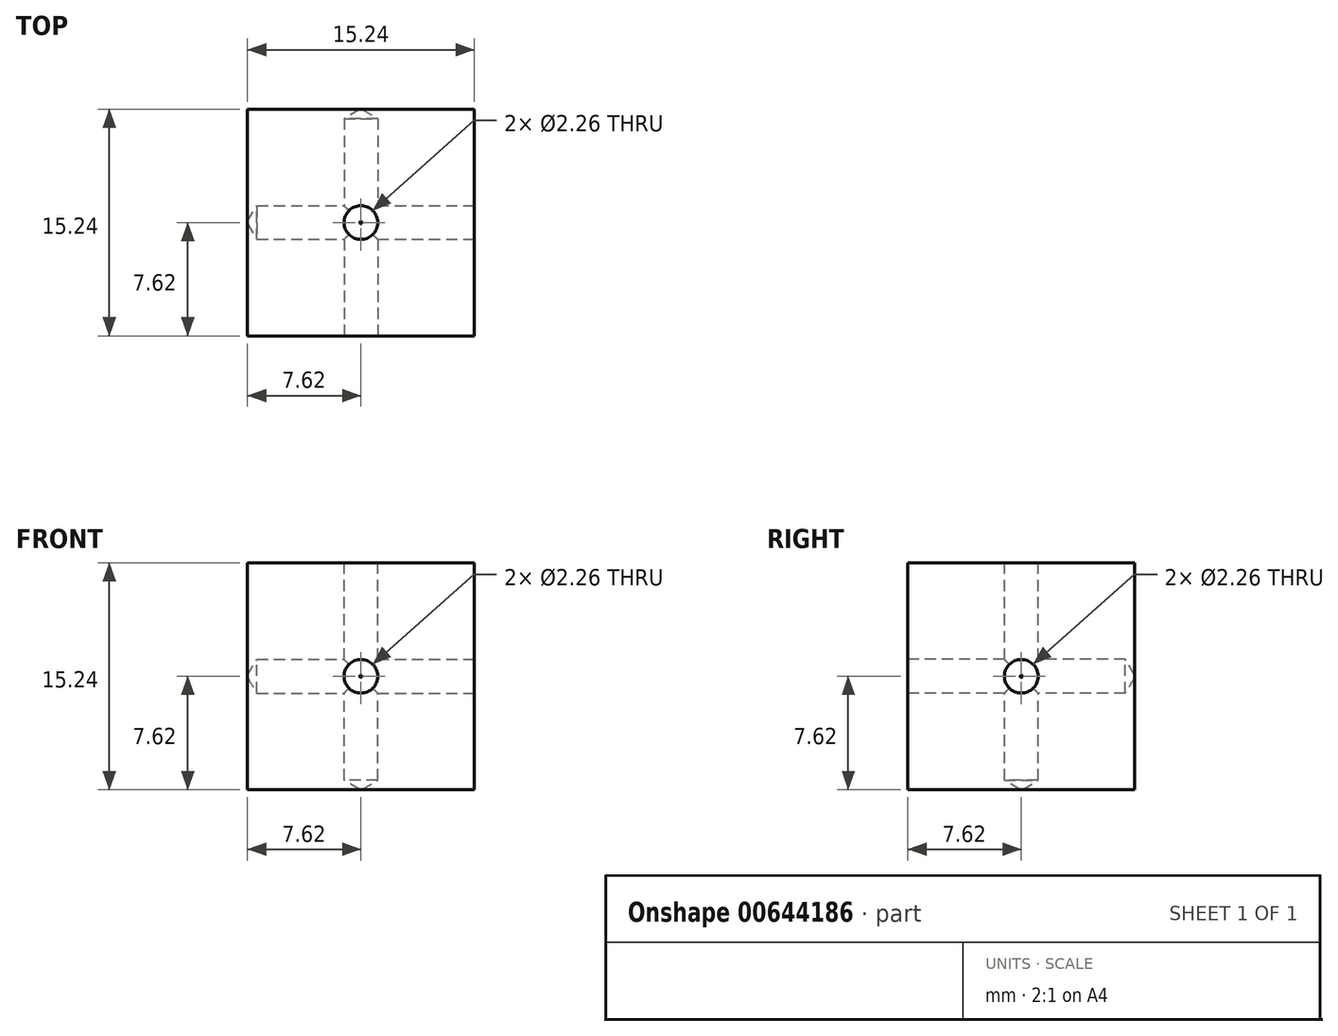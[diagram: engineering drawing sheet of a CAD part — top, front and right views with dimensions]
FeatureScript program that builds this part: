
annotation { "Feature Type Name" : "Feature", "Feature Type Description" : "" }
export const myFeature = defineFeature(function(context is Context, id is Id, definition is map)
    precondition{}
    {
        {
            var Q0;
            Q0=qCreatedBy(makeId("Front.planeOp"),FACE);
            var sketch = newSketch(context, id + "F0", { "sketchPlane" : qUnion([Q0])});
            skLineSegment(sketch, "E0.bottom", {"start": v(-7.62, 7.62) * mm, "end": v(7.62, 7.62) * mm});
            skLineSegment(sketch, "E0.top", {"start": v(-7.62, -7.62) * mm, "end": v(7.62, -7.62) * mm});
            skLineSegment(sketch, "E0.left", {"start": v(-7.62, 7.62) * mm, "end": v(-7.62, -7.62) * mm});
            skLineSegment(sketch, "E0.right", {"start": v(7.62, 7.62) * mm, "end": v(7.62, -7.62) * mm});
            skPoint(sketch, "E0.middle", {"position": v(0, 0) * mm});
            skSolve(sketch);
        }
        {
            var Q0;
            Q0=makeQuery(id+"F0.imprint","IMPRINT",FACE,{"disambiguationData":[TD([[makeQuery(id+"F0.imprint","IMPRINT",EDGE,{"derivedFrom":sQuery(id+"F0.wireOp",EDGE,"E0.bottom")}),-1.0]])]});
            extrude(context, id + "F1", {"entities" : qUnion([Q0]), "depth" : 15.24 * mm, "offsetDistance" : 25.4 * mm});
        }
        {
            var Q0;
            Q0=makeQuery(id+"F1.opExtrude","CAP_FACE",FACE,{"disambiguationData":[OSD([sQuery(id+"F0.wireOp",EDGE,"E0.bottom"),sQuery(id+"F0.wireOp",EDGE,"E0.top"),sQuery(id+"F0.wireOp",EDGE,"E0.left"),sQuery(id+"F0.wireOp",EDGE,"E0.right")])],"isStart":false});
            var sketch = newSketch(context, id + "F2", { "sketchPlane" : qUnion([Q0])});
            skPoint(sketch, "E1", {"position": v(0, 0) * mm});
            skSolve(sketch);
        }
        {
            var Q0;
            Q0=sQuery(id+"F2.wireOp",VERTEX,"E1");
            var Q1;
            Q1=makeQuery(id+"F1.opExtrude","SWEPT_BODY",BODY,{"disambiguationData":[OSD([sQuery(id+"F0.wireOp",EDGE,"E0.bottom"),sQuery(id+"F0.wireOp",EDGE,"E0.top"),sQuery(id+"F0.wireOp",EDGE,"E0.left"),sQuery(id+"F0.wireOp",EDGE,"E0.right")])]});
            hole(context, id + "F3", {"style" : HoleStyle.SIMPLE, "endStyle" : HoleEndStyle.BLIND, "standardTappedOrClearance" : lookupTablePath({ "standard" : "ANSI", "engagement" : "75%", "pitch" : "40 tpi", "size" : "#4", "type" : "Tapped" }), "standardBlindInLast" : lookupTablePath({ "standard" : "ANSI", "engagement" : "75%", "pitch" : "40 tpi", "size" : "#4", "type" : "Tapped" }), "holeDiameter" : 2.26 * mm, "majorDiameter" : 2.84 * mm, "showTappedDepth" : true, "holeDepth" : 14.6 * mm, "isTappedThrough" : true, "tappedDepth" : 12.7 * mm, "tapClearance" : 3, "locations" : qUnion([Q0]), "scope" : qUnion([Q1])});
        }
        {
            var Q0;
            Q0=makeQuery(id+"F1.opExtrude","SWEPT_FACE",FACE,{"disambiguationData":[OSD([sQuery(id+"F0.wireOp",EDGE,"E0.right")])]});
            var sketch = newSketch(context, id + "F4", { "sketchPlane" : qUnion([Q0])});
            skPoint(sketch, "E2", {"position": v(-7.62, 0) * mm});
            skPoint(sketch, "E2.positionSnap0", {"position": v(-7.62, 7.62) * mm});
            skSolve(sketch);
        }
        {
            var Q0;
            Q0=makeQuery(id+"F1.opExtrude","SWEPT_FACE",FACE,{"disambiguationData":[OSD([sQuery(id+"F0.wireOp",EDGE,"E0.bottom")])]});
            var sketch = newSketch(context, id + "F5", { "sketchPlane" : qUnion([Q0])});
            skPoint(sketch, "E3", {"position": v(0, -7.62) * mm});
            skPoint(sketch, "E3.positionSnap0", {"position": v(0, -15.24) * mm});
            skPoint(sketch, "E3.positionSnap1", {"position": v(7.62, -7.62) * mm});
            skSolve(sketch);
        }
        {
            var Q0;
            Q0=sQuery(id+"F4.wireOp",VERTEX,"E2");
            var Q1;
            Q1=makeQuery(id+"F1.opExtrude","SWEPT_BODY",BODY,{"disambiguationData":[OSD([sQuery(id+"F0.wireOp",EDGE,"E0.bottom"),sQuery(id+"F0.wireOp",EDGE,"E0.top"),sQuery(id+"F0.wireOp",EDGE,"E0.left"),sQuery(id+"F0.wireOp",EDGE,"E0.right")])]});
            hole(context, id + "F6", {"style" : HoleStyle.SIMPLE, "endStyle" : HoleEndStyle.BLIND, "standardTappedOrClearance" : lookupTablePath({ "standard" : "ANSI", "engagement" : "75%", "pitch" : "40 tpi", "size" : "#4", "type" : "Tapped" }), "standardBlindInLast" : lookupTablePath({ "standard" : "ANSI", "engagement" : "75%", "pitch" : "40 tpi", "size" : "#4", "type" : "Tapped" }), "holeDiameter" : 2.26 * mm, "majorDiameter" : 2.84 * mm, "showTappedDepth" : true, "holeDepth" : 14.6 * mm, "isTappedThrough" : true, "tappedDepth" : 12.7 * mm, "tapClearance" : 3, "locations" : qUnion([Q0]), "scope" : qUnion([Q1])});
        }
        {
            var Q0;
            Q0=sQuery(id+"F5.wireOp",VERTEX,"E3");
            var Q1;
            Q1=makeQuery(id+"F1.opExtrude","SWEPT_BODY",BODY,{"disambiguationData":[OSD([sQuery(id+"F0.wireOp",EDGE,"E0.bottom"),sQuery(id+"F0.wireOp",EDGE,"E0.top"),sQuery(id+"F0.wireOp",EDGE,"E0.left"),sQuery(id+"F0.wireOp",EDGE,"E0.right")])]});
            hole(context, id + "F7", {"style" : HoleStyle.SIMPLE, "endStyle" : HoleEndStyle.BLIND, "standardTappedOrClearance" : lookupTablePath({ "standard" : "ANSI", "engagement" : "75%", "pitch" : "40 tpi", "size" : "#4", "type" : "Tapped" }), "standardBlindInLast" : lookupTablePath({ "standard" : "ANSI", "engagement" : "75%", "pitch" : "40 tpi", "size" : "#4", "type" : "Tapped" }), "holeDiameter" : 2.26 * mm, "majorDiameter" : 2.84 * mm, "showTappedDepth" : true, "holeDepth" : 14.6 * mm, "isTappedThrough" : true, "tappedDepth" : 12.7 * mm, "tapClearance" : 3, "locations" : qUnion([Q0]), "scope" : qUnion([Q1])});
        }
    });
